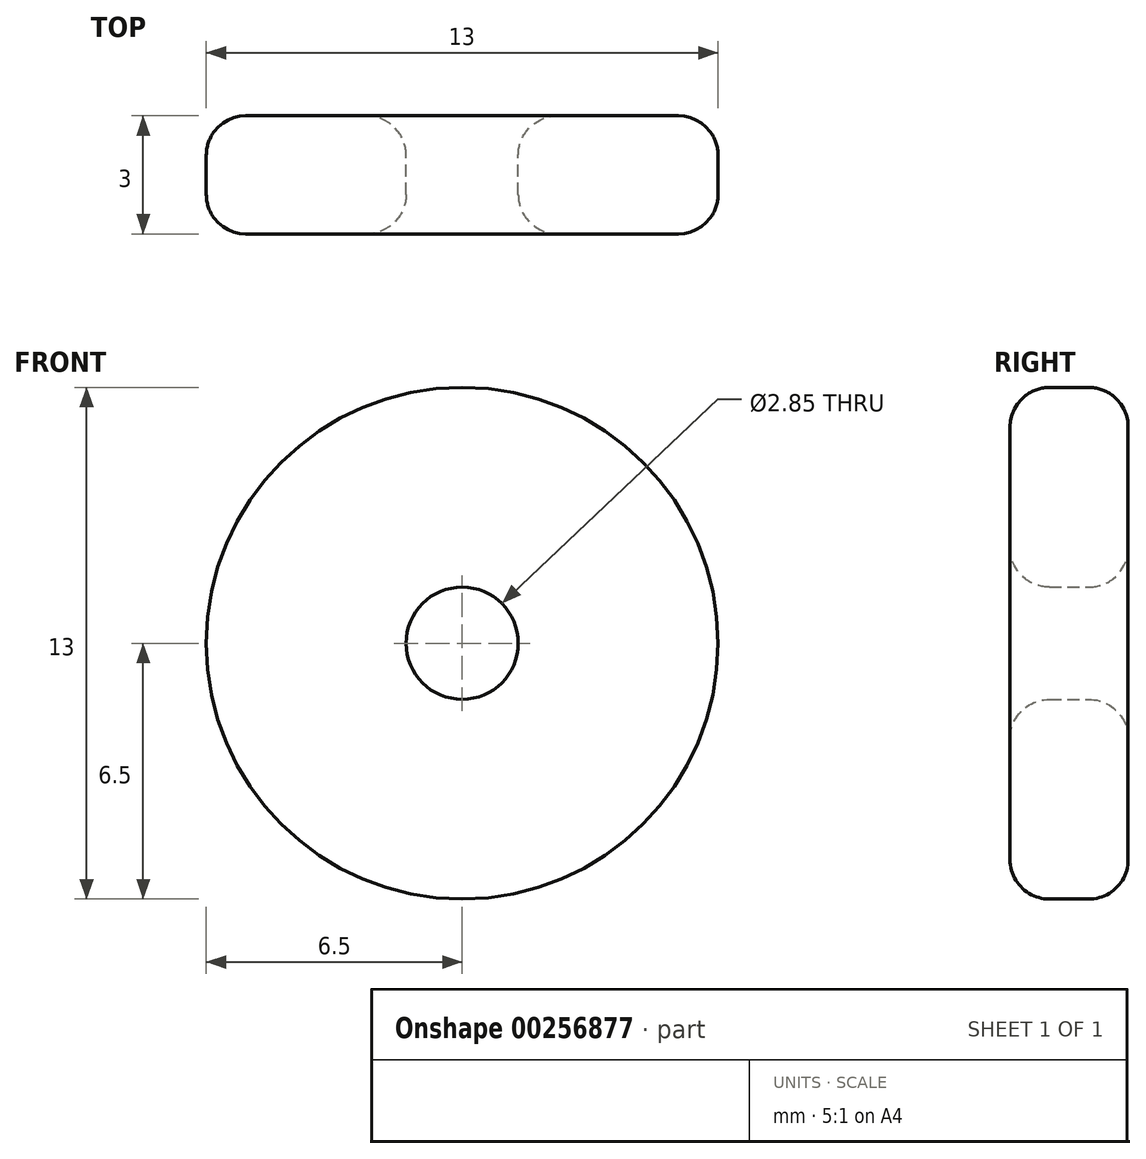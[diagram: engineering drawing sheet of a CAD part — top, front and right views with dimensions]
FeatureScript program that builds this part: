
annotation { "Feature Type Name" : "Feature", "Feature Type Description" : "" }
export const myFeature = defineFeature(function(context is Context, id is Id, definition is map)
    precondition{}
    {
        {
            var Q0;
            Q0=qCreatedBy(makeId("Front.planeOp"),FACE);
            var sketch = newSketch(context, id + "F0", { "sketchPlane" : qUnion([Q0])});
            skCircle(sketch, "E0", {"center": v(0, 0) * mm, "radius": 6.5 * mm});
            skCircle(sketch, "E1", {"center": v(0, 0) * mm, "radius": 1.43 * mm});
            skSolve(sketch);
        }
        {
            var Q0;
            Q0=makeQuery(id+"F0.imprint","IMPRINT",FACE,{"disambiguationData":[TD([[makeQuery(id+"F0.imprint","IMPRINT",EDGE,{"derivedFrom":sQuery(id+"F0.wireOp",EDGE,"E0")}),1.0]])]});
            extrude(context, id + "F1", {"entities" : qUnion([Q0]), "depth" : 3 * mm});
        }
        {
            var Q0;
            Q0=makeQuery(id+"F1.opExtrude","CAP_EDGE",EDGE,{"disambiguationData":[OSD([sQuery(id+"F0.wireOp",EDGE,"E1")])],"isStart":false});
            fillet(context, id + "F2", {"entities" : qUnion([Q0]), "radius" : 1 * mm, "tangentPropagation" : true, "allowEdgeOverflow" : false});
        }
        {
            var Q0;
            Q0=makeQuery(id+"F1.opExtrude","CAP_EDGE",EDGE,{"disambiguationData":[OSD([sQuery(id+"F0.wireOp",EDGE,"E1")])],"isStart":true});
            fillet(context, id + "F3", {"entities" : qUnion([Q0]), "radius" : 1 * mm, "tangentPropagation" : true, "allowEdgeOverflow" : false});
        }
        {
            var Q0;
            Q0=makeQuery(id+"F1.opExtrude","CAP_EDGE",EDGE,{"disambiguationData":[OSD([sQuery(id+"F0.wireOp",EDGE,"E0")])],"isStart":true});
            fillet(context, id + "F4", {"entities" : qUnion([Q0]), "radius" : 1 * mm, "tangentPropagation" : true, "allowEdgeOverflow" : false});
        }
        {
            var Q0;
            Q0=makeQuery(id+"F1.opExtrude","CAP_EDGE",EDGE,{"disambiguationData":[OSD([sQuery(id+"F0.wireOp",EDGE,"E0")])],"isStart":false});
            fillet(context, id + "F5", {"entities" : qUnion([Q0]), "radius" : 1 * mm, "tangentPropagation" : true, "allowEdgeOverflow" : false});
        }
    });
